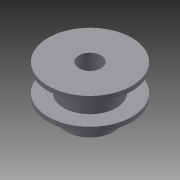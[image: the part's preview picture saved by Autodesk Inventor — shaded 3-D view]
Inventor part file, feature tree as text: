
AUTODESK INVENTOR PART (.ipt)
format: ipt  version: 2015 (Build 190159000, 159)  size: 115,712 bytes
history: native  units: mm
features: sketch x2, revolve x1, hole x1
ambient origin geometry x8: Origin, YZ Plane, XZ Plane, XY Plane, X Axis, Y Axis, Z Axis, Center Point
bodies: Solid1 (feature_tree)
feature tree (4):
  revolve  "Revolution1"  [1 undecoded]
  hole  "Hole1"  [1 undecoded]
  sketch  "Sketch1"  dims[d0=30.0mm d1=17.5mm]
  sketch  "Sketch2"  dims[d2=8.0mm d3=11.2mm d4=8.0mm d5=17.0mm d6=18.89mm d7=90.0deg d8=3.0mm d9=2.459mm d10=6.0mm d11=4.0mm d12=2.0mm d13=90.0deg d14=8.0mm d15=20.594885mm]
note: 2 required parameter values undecoded (feature->parameter linkage not recoverable at this tier; creation-order binding heuristic only, values carry confidence <= 0.55)